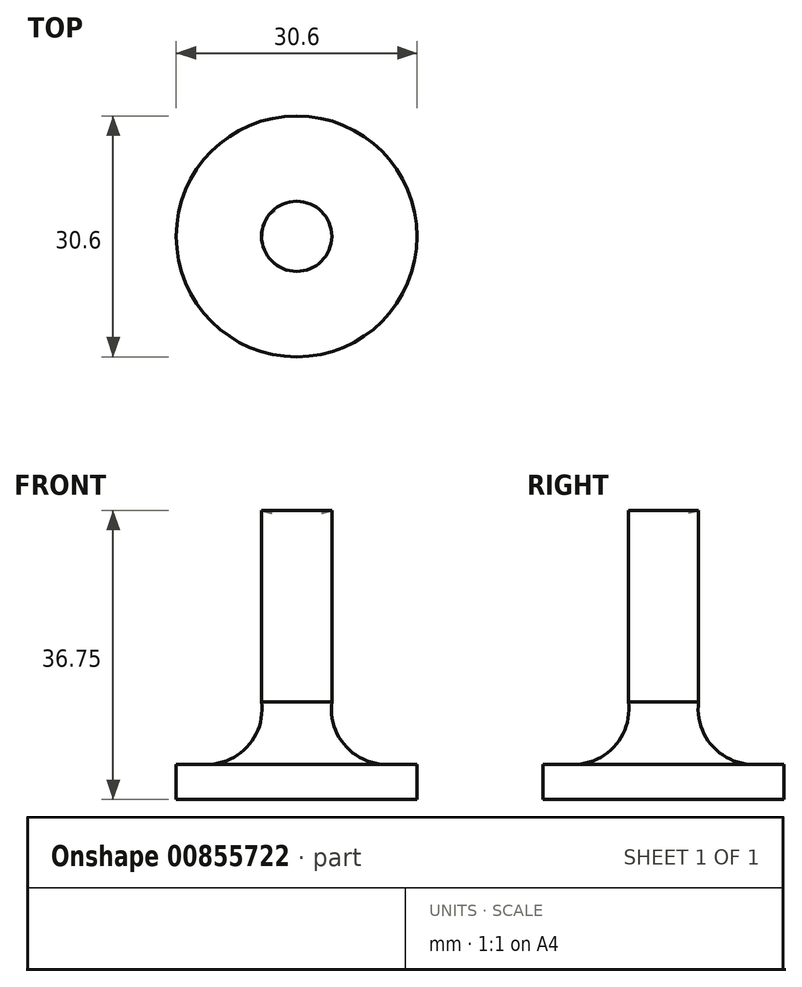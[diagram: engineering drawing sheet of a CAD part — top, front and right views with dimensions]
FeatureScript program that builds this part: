
annotation { "Feature Type Name" : "Feature", "Feature Type Description" : "" }
export const myFeature = defineFeature(function(context is Context, id is Id, definition is map)
    precondition{}
    {
        {
            var Q0;
            Q0=qCreatedBy(makeId("Front.planeOp"),FACE);
            var sketch = newSketch(context, id + "F0", { "sketchPlane" : qUnion([Q0])});
            skLineSegment(sketch, "E0", {"start": v(0, 0) * mm, "end": v(0, 63.26) * mm, "construction": true});
            skLineSegment(sketch, "E1", {"start": v(0, 0) * mm, "end": v(-15.3, 0) * mm});
            skLineSegment(sketch, "E2", {"start": v(-15.3, 0) * mm, "end": v(-15.3, 4.46) * mm});
            skLineSegment(sketch, "E3", {"start": v(-15.3, 4.46) * mm, "end": v(-11.45, 4.46) * mm});
            skArc(sketch, "E4", {"start": v(-11.45, 4.46) * mm, "mid": v(-6.15, 6.85) * mm, "end": v(-4.46, 12.41) * mm});
            skLineSegment(sketch, "E5", {"start": v(-4.46, 12.41) * mm, "end": v(-4.46, 36.75) * mm});
            skArc(sketch, "E6", {"start": v(0, 52.9) * mm, "mid": v(-9.68, 46.88) * mm, "end": v(-4.46, 36.75) * mm});
            skLineSegment(sketch, "E7", {"start": v(0, 52.9) * mm, "end": v(0, 0) * mm});
            skSolve(sketch);
        }
        {
            var Q0;
            Q0=makeQuery(id+"F0.imprint","IMPRINT",FACE,{"disambiguationData":[TD([[makeQuery(id+"F0.imprint","IMPRINT",EDGE,{"derivedFrom":sQuery(id+"F0.wireOp",EDGE,"E1")}),-1.0]])]});
            var Q1;
            Q1=sQuery(id+"F0.wireOp",EDGE,"E7");
            revolve(context, id + "F1", {"surfaceOperationType" : NewSurfaceOperationType.NEW, "entities" : qUnion([Q0]), "axis" : qUnion([Q1]), "revolveType" : RevolveType.FULL});
        }
    });
